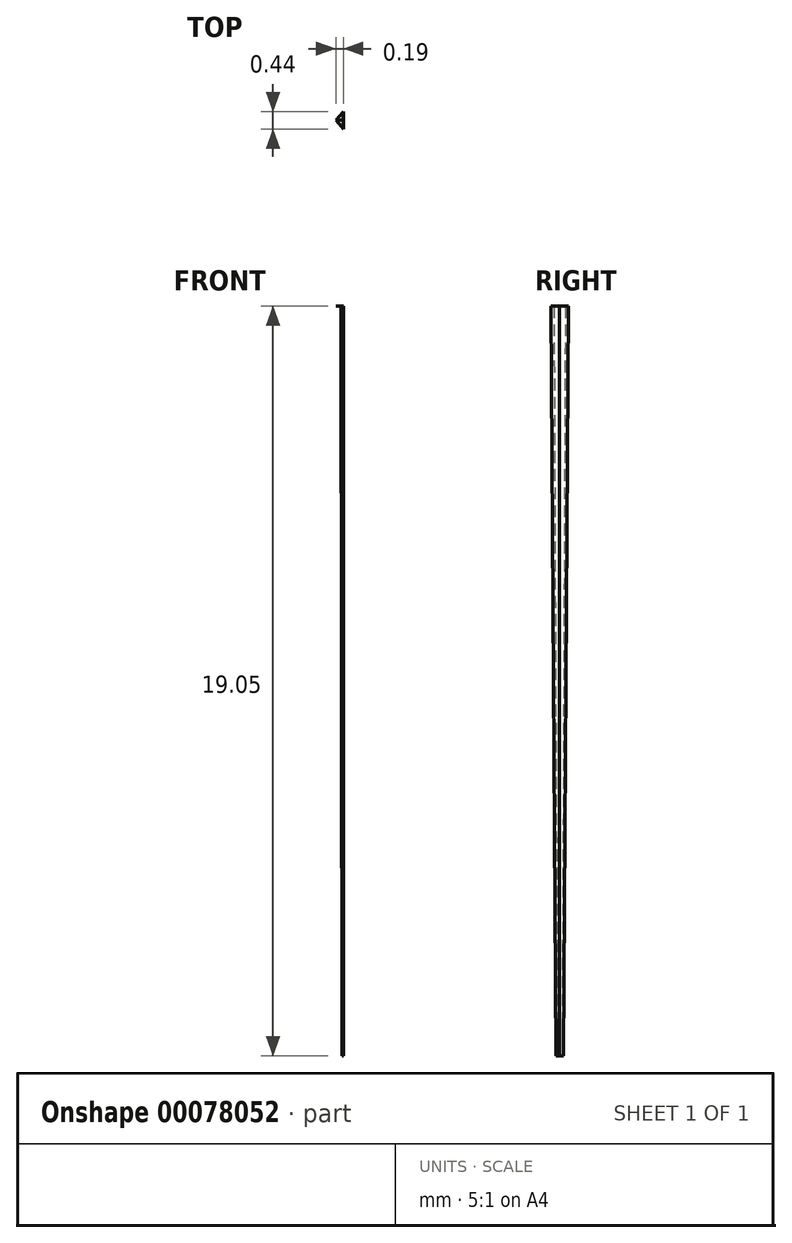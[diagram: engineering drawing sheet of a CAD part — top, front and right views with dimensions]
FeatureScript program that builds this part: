
annotation { "Feature Type Name" : "Feature", "Feature Type Description" : "" }
export const myFeature = defineFeature(function(context is Context, id is Id, definition is map)
    precondition{}
    {
        {
            var Q0;
            Q0=qCreatedBy(makeId("Front.planeOp"),FACE);
            var sketch = newSketch(context, id + "F0", { "sketchPlane" : qUnion([Q0])});
            skLineSegment(sketch, "E0.bottom", {"start": v(41.28, -9.53) * mm, "end": v(-41.27, -9.53) * mm});
            skLineSegment(sketch, "E0.top", {"start": v(41.27, 9.53) * mm, "end": v(-41.28, 9.52) * mm});
            skLineSegment(sketch, "E0.left", {"start": v(41.28, -9.53) * mm, "end": v(41.28, 9.53) * mm});
            skLineSegment(sketch, "E0.right", {"start": v(-41.27, -9.53) * mm, "end": v(-41.28, 9.52) * mm});
            skPoint(sketch, "E0.middle", {"position": v(0, 0) * mm});
            skLineSegment(sketch, "E1.bottom", {"start": v(111.13, 34.93) * mm, "end": v(60.33, 34.92) * mm});
            skLineSegment(sketch, "E1.top", {"start": v(111.13, 66.68) * mm, "end": v(60.33, 66.68) * mm});
            skLineSegment(sketch, "E1.left", {"start": v(111.13, 34.93) * mm, "end": v(111.13, 66.67) * mm});
            skLineSegment(sketch, "E1.right", {"start": v(60.33, 34.92) * mm, "end": v(60.33, 66.67) * mm});
            skPoint(sketch, "E1.middle", {"position": v(85.73, 50.8) * mm});
            skLineSegment(sketch, "E2", {"start": v(41.27, 9.53) * mm, "end": v(41.27, 27) * mm});
            skArc(sketch, "E3", {"start": v(41.27, 27) * mm, "mid": v(45.92, 38.23) * mm, "end": v(57.15, 42.88) * mm});
            skLineSegment(sketch, "E4", {"start": v(57.15, 42.88) * mm, "end": v(85.98, 42.88) * mm});
            skLineSegment(sketch, "E5.0", {"start": v(57.15, 61.93) * mm, "end": v(85.98, 61.93) * mm});
            skArc(sketch, "E5.1", {"start": v(22.23, 27) * mm, "mid": v(32.45, 51.7) * mm, "end": v(57.15, 61.93) * mm});
            skLineSegment(sketch, "E5.2", {"start": v(22.23, 9.53) * mm, "end": v(22.23, 27) * mm});
            skLineSegment(sketch, "E6", {"start": v(85.98, 61.93) * mm, "end": v(85.98, 42.88) * mm});
            skFitSpline(sketch, "E7", {"points": [v(-41.28, 9.52) * mm, v(57.15, 61.93) * mm], "startDerivative": vector(-0.68, 52.62) * mm, "endDerivative": vector(126.47, 0.76) * mm});
            skLineSegment(sketch, "E8", {"start": v(85.73, 73.8) * mm, "end": v(85.98, 27.66) * mm});
            skSolve(sketch);
        }
        {
            var Q0;
            Q0=makeQuery(id+"F0.imprint","IMPRINT",FACE,{"disambiguationData":[TD([[makeQuery(id+"F0.imprint","IMPRINT",EDGE,{"derivedFrom":sQuery(id+"F0.wireOp",EDGE,"E0.bottom")}),-1.0]])]});
            extrude(context, id + "F1", {"entities" : qUnion([Q0]), "endBound" : BoundingType.SYMMETRIC, "depth" : 127 * mm});
        }
        {
            var Q0;
            {var subQ1=sQuery(id+"F0.wireOp",EDGE,"E2");Q0=makeQuery(id+"F0.imprint","IMPRINT",FACE,{"disambiguationData":[TD([[makeQuery(id+"F0.imprint","IMPRINT",EDGE,{"derivedFrom":subQ1}),1.0]])]});}
            var Q1;
            {var subQ5=sQuery(id+"F0.wireOp",EDGE,"E6");Q1=makeQuery(id+"F0.imprint","IMPRINT",FACE,{"disambiguationData":[TD([[makeQuery(id+"F0.imprint","IMPRINT",EDGE,{"derivedFrom":subQ5}),-1.0]])]});}
            extrude(context, id + "F2", {"entities" : qUnion([Q0, Q1]), "operationType" : NewBodyOperationType.ADD, "endBound" : BoundingType.SYMMETRIC, "depth" : 50.8 * mm});
        }
        {
            var Q0;
            {var subQ3=sQuery(id+"F0.wireOp",EDGE,"E5.2");Q0=makeQuery(id+"F0.imprint","IMPRINT",FACE,{"disambiguationData":[TD([[makeQuery(id+"F0.imprint","IMPRINT",EDGE,{"derivedFrom":subQ3}),1.0]])]});}
            extrude(context, id + "F3", {"entities" : qUnion([Q0]), "operationType" : NewBodyOperationType.ADD, "endBound" : BoundingType.SYMMETRIC, "depth" : 15.88 * mm});
        }
        {
            var Q0;
            {var subQ0=sQuery(id+"F0.wireOp",EDGE,"E4");var subQ1=sQuery(id+"F0.wireOp",EDGE,"E1.right");var subQ2=makeQuery(id+"F0.imprint","INTERSECT",VERTEX,{"derivedFrom":[subQ1,subQ0]});Q0=makeQuery(id+"F0.imprint","IMPRINT",FACE,{"disambiguationData":[TD([[makeQuery(id+"F0.imprint","IMPRINT",EDGE,{"disambiguationData":[TD([[subQ2,-1.0]])],"derivedFrom":subQ1}),-1.0]])]});}
            extrude(context, id + "F4", {"entities" : qUnion([Q0]), "endBound" : BoundingType.SYMMETRIC, "depth" : 50.8 * mm});
        }
        {
            var Q0;
            {var subQ4=sQuery(id+"F0.wireOp",EDGE,"E1.left");Q0=makeQuery(id+"F0.imprint","IMPRINT",FACE,{"disambiguationData":[TD([[makeQuery(id+"F0.imprint","IMPRINT",EDGE,{"derivedFrom":subQ4}),1.0]])]});}
            var Q1;
            Q1=sQuery(id+"F0.wireOp",EDGE,"E8");
            revolve(context, id + "F5", {"operationType" : NewBodyOperationType.INTERSECT, "entities" : qUnion([Q0]), "axis" : qUnion([Q1]), "revolveType" : RevolveType.SYMMETRIC, "oppositeDirection" : true, "angle" : 98.93 * degree});
        }
    });
